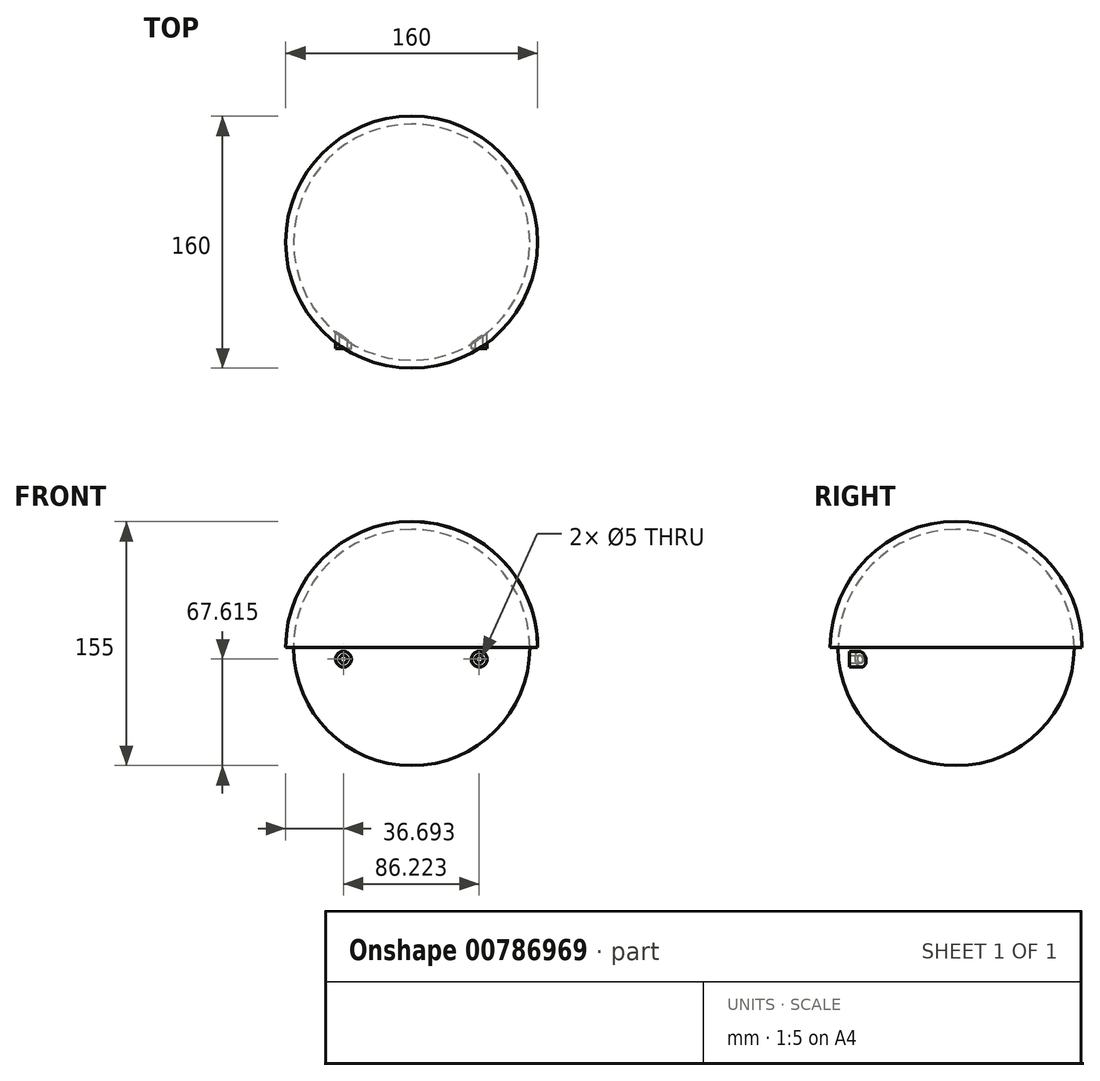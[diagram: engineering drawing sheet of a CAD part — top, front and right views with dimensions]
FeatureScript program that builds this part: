
annotation { "Feature Type Name" : "Feature", "Feature Type Description" : "" }
export const myFeature = defineFeature(function(context is Context, id is Id, definition is map)
    precondition{}
    {
        {
            var Q0;
            Q0=qCreatedBy(makeId("Front.planeOp"),FACE);
            var sketch = newSketch(context, id + "F0", { "sketchPlane" : qUnion([Q0])});
            skCircle(sketch, "E0", {"center": v(0, 0) * mm, "radius": 75 * mm});
            skLineSegment(sketch, "E1", {"start": v(0, -85.72) * mm, "end": v(0, 95.37) * mm});
            skSolve(sketch);
        }
        {
            var Q0;
            {var subQ0=sQuery(id+"F0.wireOp",EDGE,"E1");var subQ1=sQuery(id+"F0.wireOp",EDGE,"E0");var subQ2=makeQuery(id+"F0.imprint","INTERSECT",VERTEX,{"disambiguationData":[OD(0.0)],"derivedFrom":[subQ1,subQ0]});Q0=makeQuery(id+"F0.imprint","IMPRINT",FACE,{"disambiguationData":[TD([[makeQuery(id+"F0.imprint","IMPRINT",EDGE,{"disambiguationData":[TD([[subQ2,-1.0]])],"derivedFrom":subQ1}),1.0]])]});}
            var Q1;
            Q1=sQuery(id+"F0.wireOp",EDGE,"E1");
            revolve(context, id + "F1", {"surfaceOperationType" : NewSurfaceOperationType.NEW, "entities" : qUnion([Q0]), "axis" : qUnion([Q1]), "revolveType" : RevolveType.FULL});
        }
        {
            var Q0;
            Q0=qCreatedBy(makeId("Front.planeOp"),FACE);
            var sketch = newSketch(context, id + "F2", { "sketchPlane" : qUnion([Q0])});
            skCircle(sketch, "E2", {"center": v(0, 0) * mm, "radius": 80 * mm});
            skLineSegment(sketch, "E3", {"start": v(0, 0) * mm, "end": v(80, 0) * mm});
            skLineSegment(sketch, "E4", {"start": v(80, 0) * mm, "end": v(-80, 0) * mm});
            skLineSegment(sketch, "E5", {"start": v(0, -87.39) * mm, "end": v(0, 86.6) * mm});
            skSolve(sketch);
        }
        {
            var Q0;
            {var subQ0=sQuery(id+"F2.wireOp",EDGE,"E4");Q0=makeQuery(id+"F2.imprint","IMPRINT",FACE,{"disambiguationData":[TD([[makeQuery(id+"F2.imprint","IMPRINT",EDGE,{"derivedFrom":subQ0}),-1.0]])]});}
            var Q1;
            Q1=sQuery(id+"F2.wireOp",EDGE,"E5");
            revolve(context, id + "F3", {"surfaceOperationType" : NewSurfaceOperationType.NEW, "entities" : qUnion([Q0]), "axis" : qUnion([Q1]), "revolveType" : RevolveType.FULL});
        }
        {
            var Q0;
            Q0=qCreatedBy(makeId("Front.planeOp"),FACE);
            var sketch = newSketch(context, id + "F4", { "sketchPlane" : qUnion([Q0])});
            skLineSegment(sketch, "E6", {"start": v(0, 0) * mm, "end": v(0, -7.39) * mm});
            skLineSegment(sketch, "E7", {"start": v(0, -7.39) * mm, "end": v(42.92, -7.39) * mm});
            skLineSegment(sketch, "E8", {"start": v(42.92, -7.39) * mm, "end": v(-43.3, -7.39) * mm});
            skCircle(sketch, "E9", {"center": v(-43.3, -7.39) * mm, "radius": 5 * mm});
            skCircle(sketch, "E10", {"center": v(42.92, -7.39) * mm, "radius": 5 * mm});
            skCircle(sketch, "E11", {"center": v(-43.3, -7.39) * mm, "radius": 2.5 * mm});
            skCircle(sketch, "E12", {"center": v(42.92, -7.39) * mm, "radius": 2.5 * mm});
            skSolve(sketch);
        }
        {
            var Q0;
            Q0 = qSketchRegion(id + "F4", true);
            extrude(context, id + "F5", {"entities" : qUnion([Q0]), "operationType" : NewBodyOperationType.ADD, "depth" : 67.6 * mm, "offsetDistance" : 25 * mm});
        }
        {
            var Q0;
            Q0=sQuery(id+"F4.wireOp",EDGE,"E11");
            var Q1;
            Q1=sQuery(id+"F4.wireOp",EDGE,"E12");
            extrude(context, id + "F6", {"bodyType" : ToolBodyType.SURFACE, "surfaceEntities" : qUnion([Q0, Q1]), "depth" : 74.4 * mm, "offsetDistance" : 25 * mm});
        }
    });
